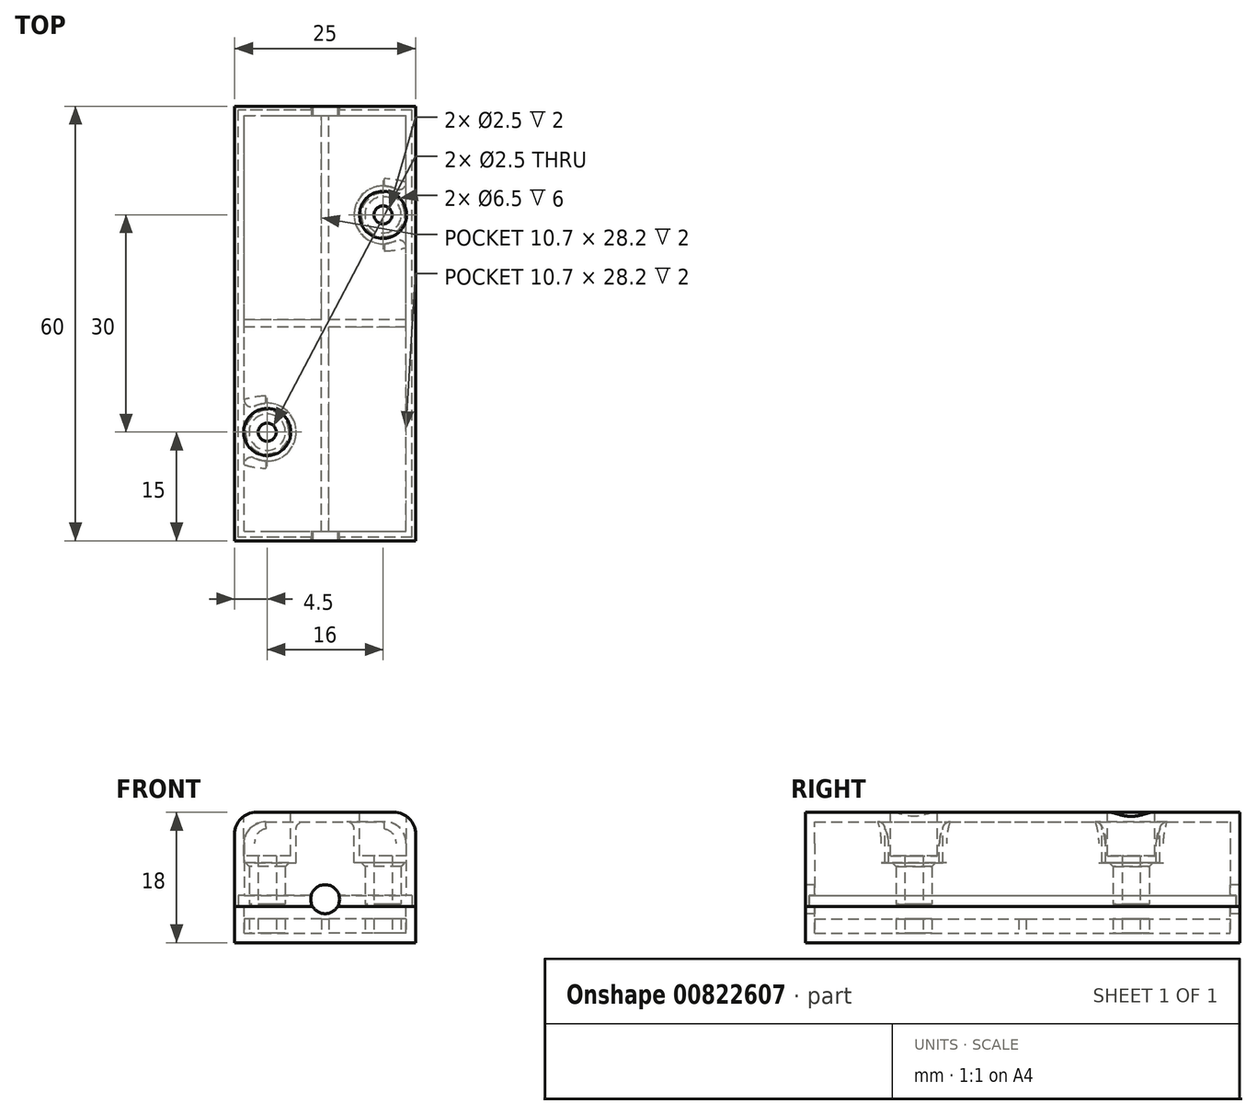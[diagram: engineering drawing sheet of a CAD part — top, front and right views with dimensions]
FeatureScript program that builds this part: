
annotation { "Feature Type Name" : "Feature", "Feature Type Description" : "" }
export const myFeature = defineFeature(function(context is Context, id is Id, definition is map)
    precondition{}
    {
        {
            var Q0;
            Q0=qCreatedBy(makeId("Front.planeOp"),FACE);
            var sketch = newSketch(context, id + "F0", { "sketchPlane" : qUnion([Q0])});
            skLineSegment(sketch, "E0.bottom", {"start": v(-12.5, -2.5) * mm, "end": v(12.5, -2.5) * mm});
            skLineSegment(sketch, "E0.top", {"start": v(-12.5, 2.5) * mm, "end": v(12.5, 2.5) * mm});
            skLineSegment(sketch, "E0.left", {"start": v(-12.5, -2.5) * mm, "end": v(-12.5, 2.5) * mm});
            skLineSegment(sketch, "E0.right", {"start": v(12.5, -2.5) * mm, "end": v(12.5, 2.5) * mm});
            skPoint(sketch, "E0.middle", {"position": v(0, 0) * mm});
            skSolve(sketch);
        }
        {
            var Q0;
            Q0 = qSketchRegion(id + "F0", true);
            extrude(context, id + "F1", {"entities" : qUnion([Q0]), "endBound" : BoundingType.SYMMETRIC, "depth" : 60 * mm, "offsetDistance" : 25 * mm});
        }
        {
            var Q0;
            Q0=makeQuery(id+"F1.opExtrude","SWEPT_FACE",FACE,{"disambiguationData":[OSD([sQuery(id+"F0.wireOp",EDGE,"E0.top")])]});
            shell(context, id + "F2", {"entities" : qUnion([Q0]), "thickness" : 1.3 * mm});
        }
        {
            var Q0;
            Q0=makeQuery(id+"F2.opShell","OFFSET_FACE",FACE,{"disambiguationData":[OSD([sQuery(id+"F0.wireOp",EDGE,"E0.bottom")])]});
            var sketch = newSketch(context, id + "F3", { "sketchPlane" : qUnion([Q0])});
            skLineSegment(sketch, "E1.bottom", {"start": v(0.5, -28.7) * mm, "end": v(-0.5, -28.7) * mm});
            skLineSegment(sketch, "E1.top", {"start": v(0.5, 28.7) * mm, "end": v(-0.5, 28.7) * mm});
            skLineSegment(sketch, "E1.left", {"start": v(0.5, -28.7) * mm, "end": v(0.5, 28.7) * mm});
            skLineSegment(sketch, "E1.right", {"start": v(-0.5, -28.7) * mm, "end": v(-0.5, 28.7) * mm});
            skPoint(sketch, "E1.middle", {"position": v(0, 0) * mm});
            skLineSegment(sketch, "E2.bottom", {"start": v(11.2, -0.5) * mm, "end": v(-11.2, -0.5) * mm});
            skLineSegment(sketch, "E2.top", {"start": v(11.2, 0.5) * mm, "end": v(-11.2, 0.5) * mm});
            skLineSegment(sketch, "E2.left", {"start": v(11.2, -0.5) * mm, "end": v(11.2, 0.5) * mm});
            skLineSegment(sketch, "E2.right", {"start": v(-11.2, -0.5) * mm, "end": v(-11.2, 0.5) * mm});
            skCircle(sketch, "E3", {"center": v(-8, -15) * mm, "radius": 2.5 * mm});
            skCircle(sketch, "E4", {"center": v(-8, -15) * mm, "radius": 1.25 * mm});
            skCircle(sketch, "E5", {"center": v(8, 15) * mm, "radius": 2.5 * mm});
            skCircle(sketch, "E6", {"center": v(8, 15) * mm, "radius": 1.25 * mm});
            skSolve(sketch);
        }
        {
            var Q0;
            Q0 = qSketchRegion(id + "F3", true);
            extrude(context, id + "F4", {"entities" : qUnion([Q0]), "operationType" : NewBodyOperationType.ADD, "depth" : 2 * mm, "offsetDistance" : 25 * mm});
        }
        {
            var Q0;
            Q0=makeQuery(id+"F1.opExtrude","SWEPT_FACE",FACE,{"disambiguationData":[OSD([sQuery(id+"F0.wireOp",EDGE,"E0.top")])]});
            var sketch = newSketch(context, id + "F5", { "sketchPlane" : qUnion([Q0])});
            skLineSegment(sketch, "E7.bottom", {"start": v(11.7, -29.2) * mm, "end": v(-11.7, -29.2) * mm});
            skLineSegment(sketch, "E7.top", {"start": v(11.7, 29.2) * mm, "end": v(-11.7, 29.2) * mm});
            skLineSegment(sketch, "E7.left", {"start": v(11.7, -29.2) * mm, "end": v(11.7, 29.2) * mm});
            skLineSegment(sketch, "E7.right", {"start": v(-11.7, -29.2) * mm, "end": v(-11.7, 29.2) * mm});
            skPoint(sketch, "E7.middle", {"position": v(0, 0) * mm});
            skSolve(sketch);
        }
        {
            var Q0;
            Q0=makeQuery(id+"F5.imprint","IMPRINT",FACE,{"disambiguationData":[TD([[makeQuery(id+"F5.imprint","IMPRINT",EDGE,{"derivedFrom":sQuery(id+"F5.wireOp",EDGE,"E7.bottom")}),-1.0]])]});
            extrude(context, id + "F6", {"entities" : qUnion([Q0]), "operationType" : NewBodyOperationType.ADD, "depth" : 1 * mm, "offsetDistance" : 25 * mm});
        }
        {
            var Q0;
            Q0=makeQuery(id+"F1.opExtrude","SWEPT_FACE",FACE,{"disambiguationData":[OSD([sQuery(id+"F0.wireOp",EDGE,"E0.top")])]});
            var sketch = newSketch(context, id + "F7", { "sketchPlane" : qUnion([Q0])});
            skLineSegment(sketch, "E8.bottom", {"start": v(-12.5, -30) * mm, "end": v(12.5, -30) * mm});
            skLineSegment(sketch, "E8.top", {"start": v(-12.5, 30) * mm, "end": v(12.5, 30) * mm});
            skLineSegment(sketch, "E8.left", {"start": v(-12.5, -30) * mm, "end": v(-12.5, 30) * mm});
            skLineSegment(sketch, "E8.right", {"start": v(12.5, -30) * mm, "end": v(12.5, 30) * mm});
            skPoint(sketch, "E8.middle", {"position": v(0, 0) * mm});
            skSolve(sketch);
        }
        {
            var Q0;
            Q0 = qSketchRegion(id + "F7", true);
            extrude(context, id + "F8", {"entities" : qUnion([Q0]), "depth" : 13 * mm, "offsetDistance" : 25 * mm});
        }
        {
            var Q0;
            Q0=makeQuery(id+"F8.opExtrude","CAP_FACE",FACE,{"disambiguationData":[OSD([sQuery(id+"F7.wireOp",EDGE,"E8.bottom"),sQuery(id+"F7.wireOp",EDGE,"E8.top"),sQuery(id+"F7.wireOp",EDGE,"E8.left"),sQuery(id+"F7.wireOp",EDGE,"E8.right")])],"isStart":true});
            shell(context, id + "F9", {"entities" : qUnion([Q0]), "thickness" : 1.3 * mm});
        }
        {
            var Q0;
            Q0=makeQuery(id+"F4.opExtrude","CAP_FACE",FACE,{"disambiguationData":[OSD([sQuery(id+"F3.wireOp",EDGE,"E3"),sQuery(id+"F3.wireOp",EDGE,"E4")])],"isStart":false});
            var Q1;
            Q1=makeQuery(id+"F4.opExtrude","CAP_FACE",FACE,{"disambiguationData":[OSD([sQuery(id+"F3.wireOp",EDGE,"E5"),sQuery(id+"F3.wireOp",EDGE,"E6")])],"isStart":false});
            extrude(context, id + "F10", {"entities" : qUnion([Q0, Q1]), "operationType" : NewBodyOperationType.ADD, "depth" : 14 * mm, "offsetDistance" : 25 * mm, "hasSecondDirection" : true, "secondDirectionOppositeDirection" : false, "secondDirectionDepth" : 2 * mm});
        }
        {
            var Q0;
            Q0=makeQuery(id+"F8.opExtrude","CAP_FACE",FACE,{"disambiguationData":[OSD([sQuery(id+"F7.wireOp",EDGE,"E8.bottom"),sQuery(id+"F7.wireOp",EDGE,"E8.top"),sQuery(id+"F7.wireOp",EDGE,"E8.left"),sQuery(id+"F7.wireOp",EDGE,"E8.right")])],"isStart":false});
            var sketch = newSketch(context, id + "F11", { "sketchPlane" : qUnion([Q0])});
            skCircle(sketch, "E9", {"center": v(-8, -15) * mm, "radius": 4 * mm});
            skCircle(sketch, "E10", {"center": v(8, 15) * mm, "radius": 4 * mm});
            skSolve(sketch);
        }
        {
            var Q0;
            Q0 = qSketchRegion(id + "F11", true);
            extrude(context, id + "F12", {"entities" : qUnion([Q0]), "operationType" : NewBodyOperationType.ADD, "oppositeDirection" : true, "depth" : 7 * mm, "offsetDistance" : 25 * mm});
        }
        {
            var Q0;
            Q0=makeQuery(id+"F8.opExtrude","CAP_FACE",FACE,{"disambiguationData":[OSD([sQuery(id+"F7.wireOp",EDGE,"E8.bottom"),sQuery(id+"F7.wireOp",EDGE,"E8.top"),sQuery(id+"F7.wireOp",EDGE,"E8.left"),sQuery(id+"F7.wireOp",EDGE,"E8.right")])],"isStart":false});
            var sketch = newSketch(context, id + "F13", { "sketchPlane" : qUnion([Q0])});
            skCircle(sketch, "E11", {"center": v(-8, -15) * mm, "radius": 3.25 * mm});
            skCircle(sketch, "E12", {"center": v(8, 15) * mm, "radius": 3.25 * mm});
            skSolve(sketch);
        }
        {
            var Q0;
            Q0 = qSketchRegion(id + "F13", true);
            extrude(context, id + "F14", {"entities" : qUnion([Q0]), "operationType" : NewBodyOperationType.REMOVE, "oppositeDirection" : true, "depth" : 6 * mm, "offsetDistance" : 25 * mm});
        }
        {
            var Q0;
            Q0=makeQuery(id+"F14.boolean.opBoolean","COPY",FACE,{"derivedFrom":makeQuery(id+"F14.opExtrude","CAP_FACE",FACE,{"disambiguationData":[OSD([sQuery(id+"F13.wireOp",EDGE,"E11")])],"isStart":false})});
            var sketch = newSketch(context, id + "F15", { "sketchPlane" : qUnion([Q0])});
            skCircle(sketch, "E13", {"center": v(-8, -15) * mm, "radius": 1.25 * mm});
            skCircle(sketch, "E14", {"center": v(8, 15) * mm, "radius": 1.25 * mm});
            skSolve(sketch);
        }
        {
            var Q0;
            Q0 = qSketchRegion(id + "F15", true);
            extrude(context, id + "F16", {"entities" : qUnion([Q0]), "operationType" : NewBodyOperationType.REMOVE, "oppositeDirection" : true, "depth" : 2.9 * mm, "offsetDistance" : 25 * mm});
        }
        {
            var Q0;
            Q0=makeQuery(id+"F8.opExtrude","CAP_EDGE",EDGE,{"disambiguationData":[OSD([sQuery(id+"F7.wireOp",EDGE,"E8.left")])],"isStart":false});
            var Q1;
            Q1=makeQuery(id+"F8.opExtrude","CAP_EDGE",EDGE,{"disambiguationData":[OSD([sQuery(id+"F7.wireOp",EDGE,"E8.right")])],"isStart":false});
            var Q2;
            {var subQ0=sQuery(id+"F7.wireOp",EDGE,"E8.left");var subQ1=sQuery(id+"F7.wireOp",EDGE,"E8.top");Q2=makeQuery(id+"F12.boolean.opBoolean","SPLIT",EDGE,{"disambiguationData":[TD([makeQuery(id+"F9.opShell","OFFSET_FACE",FACE,{"disambiguationData":[OSD([subQ1])]})])],"derivedFrom":makeQuery(id+"F9.opShell","OFFSET_EDGE",EDGE,{"disambiguationData":[OSD([subQ0]),TDD([makeQuery(id+"F8.opExtrude","CAP_EDGE",EDGE,{"disambiguationData":[OSD([subQ0])],"isStart":false})])]})});}
            var Q3;
            {var subQ0=sQuery(id+"F7.wireOp",EDGE,"E8.bottom");var subQ1=sQuery(id+"F7.wireOp",EDGE,"E8.left");Q3=makeQuery(id+"F12.boolean.opBoolean","SPLIT",EDGE,{"disambiguationData":[TD([makeQuery(id+"F9.opShell","OFFSET_FACE",FACE,{"disambiguationData":[OSD([subQ0])]})])],"derivedFrom":makeQuery(id+"F9.opShell","OFFSET_EDGE",EDGE,{"disambiguationData":[OSD([subQ1]),TDD([makeQuery(id+"F8.opExtrude","CAP_EDGE",EDGE,{"disambiguationData":[OSD([subQ1])],"isStart":false})])]})});}
            var Q4;
            {var subQ0=sQuery(id+"F7.wireOp",EDGE,"E8.bottom");var subQ1=sQuery(id+"F7.wireOp",EDGE,"E8.right");Q4=makeQuery(id+"F12.boolean.opBoolean","SPLIT",EDGE,{"disambiguationData":[TD([makeQuery(id+"F9.opShell","OFFSET_FACE",FACE,{"disambiguationData":[OSD([subQ0])]})])],"derivedFrom":makeQuery(id+"F9.opShell","OFFSET_EDGE",EDGE,{"disambiguationData":[OSD([subQ1]),TDD([makeQuery(id+"F8.opExtrude","CAP_EDGE",EDGE,{"disambiguationData":[OSD([subQ1])],"isStart":false})])]})});}
            var Q5;
            {var subQ0=sQuery(id+"F7.wireOp",EDGE,"E8.right");var subQ1=sQuery(id+"F7.wireOp",EDGE,"E8.top");Q5=makeQuery(id+"F12.boolean.opBoolean","SPLIT",EDGE,{"disambiguationData":[TD([makeQuery(id+"F9.opShell","OFFSET_FACE",FACE,{"disambiguationData":[OSD([subQ1])]})])],"derivedFrom":makeQuery(id+"F9.opShell","OFFSET_EDGE",EDGE,{"disambiguationData":[OSD([subQ0]),TDD([makeQuery(id+"F8.opExtrude","CAP_EDGE",EDGE,{"disambiguationData":[OSD([subQ0])],"isStart":false})])]})});}
            fillet(context, id + "F17", {"entities" : qUnion([Q0, Q1, Q2, Q3, Q4, Q5]), "radius" : 3 * mm, "tangentPropagation" : true, "allowEdgeOverflow" : false});
        }
        {
            var Q0;
            Q0=makeQuery(id+"F8.opExtrude","CAP_FACE",FACE,{"disambiguationData":[OSD([sQuery(id+"F7.wireOp",EDGE,"E8.bottom"),sQuery(id+"F7.wireOp",EDGE,"E8.top"),sQuery(id+"F7.wireOp",EDGE,"E8.left"),sQuery(id+"F7.wireOp",EDGE,"E8.right")])],"isStart":true});
            var sketch = newSketch(context, id + "F18", { "sketchPlane" : qUnion([Q0])});
            skLineSegment(sketch, "E15.bottom", {"start": v(12, 29.5) * mm, "end": v(-12, 29.5) * mm});
            skLineSegment(sketch, "E15.top", {"start": v(12, -29.5) * mm, "end": v(-12, -29.5) * mm});
            skLineSegment(sketch, "E15.left", {"start": v(12, 29.5) * mm, "end": v(12, -29.5) * mm});
            skLineSegment(sketch, "E15.right", {"start": v(-12, 29.5) * mm, "end": v(-12, -29.5) * mm});
            skPoint(sketch, "E15.middle", {"position": v(0, 0) * mm});
            skSolve(sketch);
        }
        {
            var Q0;
            Q0=makeQuery(id+"F18.imprint","IMPRINT",FACE,{"disambiguationData":[TD([[makeQuery(id+"F18.imprint","IMPRINT",EDGE,{"derivedFrom":sQuery(id+"F18.wireOp",EDGE,"E15.bottom")}),1.0]])]});
            extrude(context, id + "F19", {"entities" : qUnion([Q0]), "operationType" : NewBodyOperationType.REMOVE, "oppositeDirection" : true, "depth" : 1.5 * mm, "offsetDistance" : 25 * mm});
        }
        {
            var Q0;
            {var subQ0=sQuery(id+"F7.wireOp",EDGE,"E8.right");var subQ1=sQuery(id+"F7.wireOp",EDGE,"E8.left");var subQ2=sQuery(id+"F7.wireOp",EDGE,"E8.top");var subQ3=sQuery(id+"F7.wireOp",EDGE,"E8.bottom");Q0=makeQuery(id+"F12.boolean.opBoolean","INTERSECT",EDGE,{"derivedFrom":[makeQuery(id+"F10.boolean.opBoolean","SPLIT",FACE,{"disambiguationData":[TD([makeQuery(id+"F9.opShell","OFFSET_FACE",FACE,{"disambiguationData":[OSD([subQ3])]})])],"derivedFrom":makeQuery(id+"F9.opShell","OFFSET_FACE",FACE,{"disambiguationData":[OSD([subQ3,subQ2,subQ1,subQ0])]})}),makeQuery(id+"F12.opExtrude","SWEPT_FACE",FACE,{"disambiguationData":[OSD([sQuery(id+"F11.wireOp",EDGE,"E10")])]})]});}
            var Q1;
            {var subQ0=sQuery(id+"F7.wireOp",EDGE,"E8.right");var subQ1=sQuery(id+"F7.wireOp",EDGE,"E8.left");var subQ2=sQuery(id+"F7.wireOp",EDGE,"E8.top");var subQ3=sQuery(id+"F7.wireOp",EDGE,"E8.bottom");Q1=makeQuery(id+"F12.boolean.opBoolean","INTERSECT",EDGE,{"derivedFrom":[makeQuery(id+"F10.boolean.opBoolean","SPLIT",FACE,{"disambiguationData":[TD([makeQuery(id+"F9.opShell","OFFSET_FACE",FACE,{"disambiguationData":[OSD([subQ3])]})])],"derivedFrom":makeQuery(id+"F9.opShell","OFFSET_FACE",FACE,{"disambiguationData":[OSD([subQ3,subQ2,subQ1,subQ0])]})}),makeQuery(id+"F12.opExtrude","SWEPT_FACE",FACE,{"disambiguationData":[OSD([sQuery(id+"F11.wireOp",EDGE,"E9")])]})]});}
            fillet(context, id + "F20", {"entities" : qUnion([Q0, Q1]), "radius" : 1 * mm, "tangentPropagation" : true, "allowEdgeOverflow" : false});
        }
        {
            var Q0;
            Q0=makeQuery(id+"F12.boolean.opBoolean","INTERSECT",EDGE,{"derivedFrom":[makeQuery(id+"F10.opExtrude","SWEPT_FACE",FACE,{"disambiguationData":[OSD([sQuery(id+"F3.wireOp",EDGE,"E5")])]}),makeQuery(id+"F12.opExtrude","CAP_FACE",FACE,{"disambiguationData":[OSD([sQuery(id+"F11.wireOp",EDGE,"E10")])],"isStart":false})]});
            var Q1;
            Q1=makeQuery(id+"F12.boolean.opBoolean","INTERSECT",EDGE,{"derivedFrom":[makeQuery(id+"F10.opExtrude","SWEPT_FACE",FACE,{"disambiguationData":[OSD([sQuery(id+"F3.wireOp",EDGE,"E3")])]}),makeQuery(id+"F12.opExtrude","CAP_FACE",FACE,{"disambiguationData":[OSD([sQuery(id+"F11.wireOp",EDGE,"E9")])],"isStart":false})]});
            chamfer(context, id + "F21", {"entities" : qUnion([Q0, Q1]), "width" : 0.5 * mm, "tangentPropagation" : true});
        }
        {
            var Q0;
            Q0=makeQuery(id+"F8.opExtrude","SWEPT_FACE",FACE,{"disambiguationData":[OSD([sQuery(id+"F7.wireOp",EDGE,"E8.bottom")])]});
            var sketch = newSketch(context, id + "F22", { "sketchPlane" : qUnion([Q0])});
            skCircle(sketch, "E16", {"center": v(0, 3.5) * mm, "radius": 2 * mm});
            skSolve(sketch);
        }
        {
            var Q0;
            Q0 = qSketchRegion(id + "F22", true);
            extrude(context, id + "F23", {"entities" : qUnion([Q0]), "operationType" : NewBodyOperationType.REMOVE, "oppositeDirection" : true, "depth" : 66.9 * mm, "offsetDistance" : 25 * mm});
        }
    });
